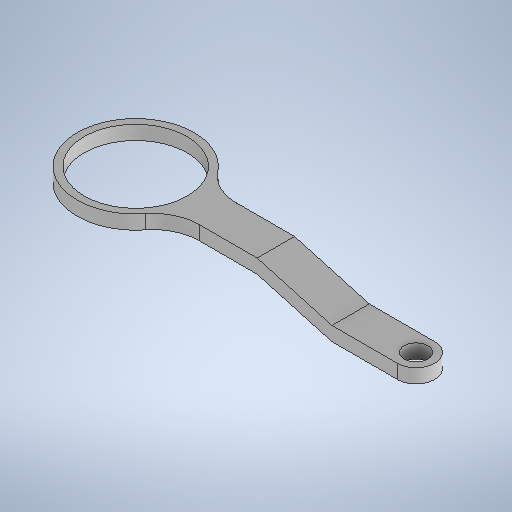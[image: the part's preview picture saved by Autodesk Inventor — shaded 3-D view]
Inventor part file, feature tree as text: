
AUTODESK INVENTOR PART (.ipt)
format: ipt  version: 2025.1 (Build 291241000, 241)  size: 297,472 bytes
history: native  units: mm
features: sketch x4, extrude x3, plane x1, hole x1
ambient origin geometry x8: Origin, YZ Plane, XZ Plane, XY Plane, X Axis, Y Axis, Z Axis, Center Point
bodies: Solid1 (feature_tree)
feature tree (9):
  sketch  "Sketch1"  dims[d0=25.0mm d1=22.0mm]
  extrude  "Extrusion1"  Depth=22.0mm
  plane  "Work Plane3"
  extrude  "Extrusion3"  Depth=10.0mm
  extrude  "Extrusion4"  Depth=3.0mm TaperAngle=0.0deg
  hole  "Hole1"  [1 undecoded]
  sketch  "Sketch7"  dims[d2=4.0mm d3=10.0mm]
  sketch  "Sketch8"  dims[d4=60.0mm d5=3.0mm d6=0.0mm]
  sketch  "Sketch9"  dims[d17=42.5mm d18=0.0mm d19=4.5mm d20=14.0mm d21=60.0mm d22=3.0mm d23=8.0mm d24=0.0mm d25=4.0mm d26=8.0mm d27=0.0mm d28=5.0mm d29=6.0mm d30=4.0mm d31=2.0mm d32=90.0deg d33=8.0mm d34=0.0mm]
note: 1 required parameter value undecoded (feature->parameter linkage not recoverable at this tier; creation-order binding heuristic only, values carry confidence <= 0.55)
